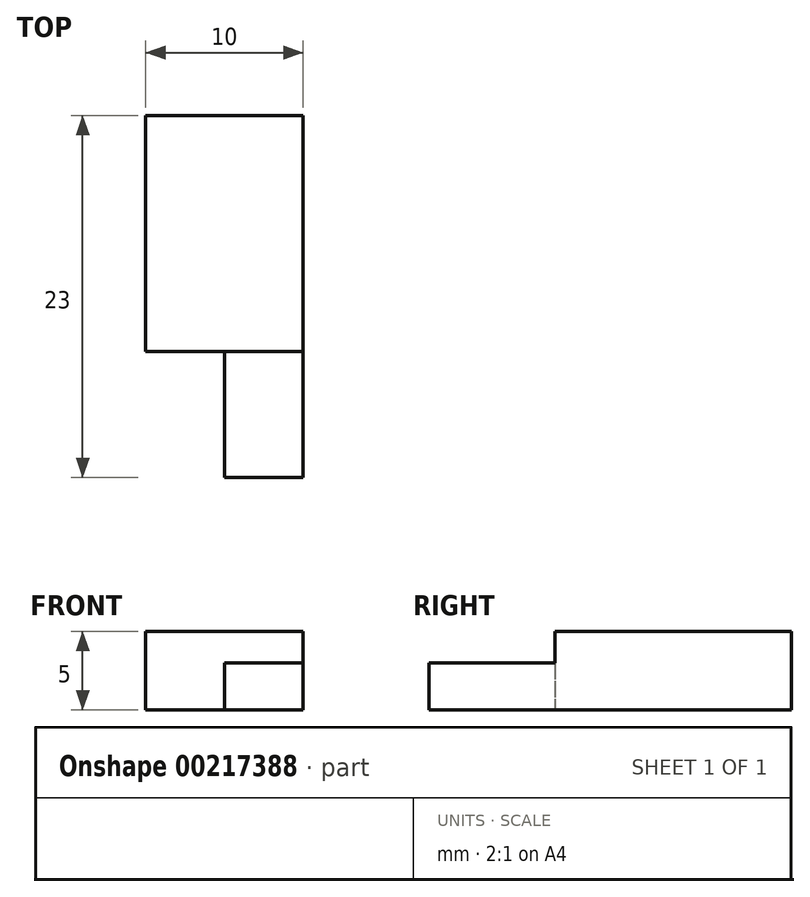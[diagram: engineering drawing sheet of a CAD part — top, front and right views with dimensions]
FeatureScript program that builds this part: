
annotation { "Feature Type Name" : "Feature", "Feature Type Description" : "" }
export const myFeature = defineFeature(function(context is Context, id is Id, definition is map)
    precondition{}
    {
        {
            var Q0;
            Q0=qCreatedBy(makeId("Top.planeOp"),FACE);
            var sketch = newSketch(context, id + "F0", { "sketchPlane" : qUnion([Q0])});
            skLineSegment(sketch, "E0", {"start": v(0, 0) * mm, "end": v(10, 0) * mm});
            skLineSegment(sketch, "E1", {"start": v(10, 0) * mm, "end": v(10, 15) * mm});
            skLineSegment(sketch, "E2", {"start": v(10, 15) * mm, "end": v(0, 15) * mm});
            skLineSegment(sketch, "E3", {"start": v(0, 15) * mm, "end": v(0, 0) * mm});
            skSolve(sketch);
        }
        {
            var Q0;
            Q0=makeQuery(id+"F0.imprint","IMPRINT",FACE,{"disambiguationData":[TD([[makeQuery(id+"F0.imprint","IMPRINT",EDGE,{"derivedFrom":sQuery(id+"F0.wireOp",EDGE,"E0")}),1.0]])]});
            extrude(context, id + "F1", {"entities" : qUnion([Q0]), "depth" : 5 * mm});
        }
        {
            var Q0;
            Q0=makeQuery(id+"F1.opExtrude","SWEPT_FACE",FACE,{"disambiguationData":[OSD([sQuery(id+"F0.wireOp",EDGE,"E0")])]});
            var sketch = newSketch(context, id + "F2", { "sketchPlane" : qUnion([Q0])});
            skLineSegment(sketch, "E4", {"start": v(10, 0) * mm, "end": v(10, 3) * mm});
            skLineSegment(sketch, "E5", {"start": v(10, 3) * mm, "end": v(5, 3) * mm});
            skLineSegment(sketch, "E6", {"start": v(5, 3) * mm, "end": v(5, 0) * mm});
            skLineSegment(sketch, "E7", {"start": v(5, 0) * mm, "end": v(10, 0) * mm});
            skSolve(sketch);
        }
        {
            var Q0;
            Q0 = qSketchRegion(id + "F2", true);
            extrude(context, id + "F3", {"entities" : qUnion([Q0]), "operationType" : NewBodyOperationType.ADD, "depth" : 8 * mm});
        }
    });
